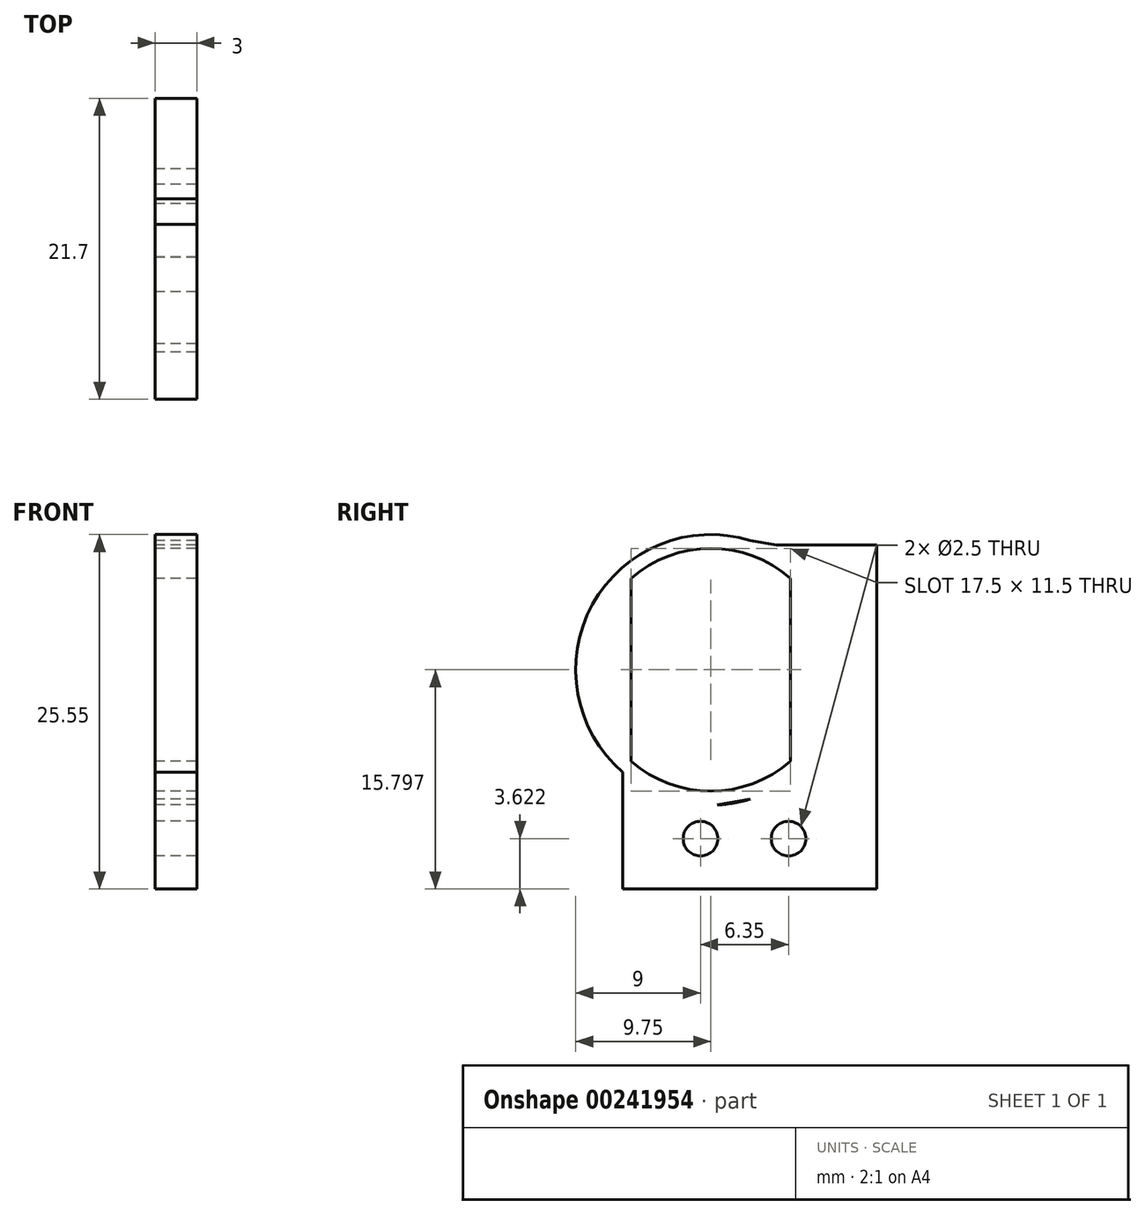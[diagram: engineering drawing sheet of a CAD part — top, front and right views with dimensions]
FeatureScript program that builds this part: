
annotation { "Feature Type Name" : "Feature", "Feature Type Description" : "" }
export const myFeature = defineFeature(function(context is Context, id is Id, definition is map)
    precondition{}
    {
        {
            var Q0;
            Q0=qCreatedBy(makeId("Right.planeOp"),FACE);
            var sketch = newSketch(context, id + "F0", { "sketchPlane" : qUnion([Q0])});
            skLineSegment(sketch, "E0", {"start": v(-11.95, -13.7) * mm, "end": v(-11.95, -5.31) * mm});
            skCircle(sketch, "E1", {"center": v(-5.6, 2.09) * mm, "radius": 9.75 * mm});
            skCircle(sketch, "E2", {"center": v(-5.6, 2.09) * mm, "radius": 8.75 * mm});
            skLineSegment(sketch, "E3", {"start": v(-5.6, 2.09) * mm, "end": v(6.35, 2.09) * mm, "construction": true});
            skLineSegment(sketch, "E4", {"start": v(-0.03, 10.09) * mm, "end": v(5.35, 10.09) * mm});
            skLineSegment(sketch, "E5", {"start": v(5.35, 10.09) * mm, "end": v(5.35, 2.09) * mm});
            skLineSegment(sketch, "E6.MirrorCS", {"start": v(5.35, -5.91) * mm, "end": v(5.35, 2.09) * mm});
            skLineSegment(sketch, "E7.MirrorCS", {"start": v(-0.03, -5.91) * mm, "end": v(5.35, -5.91) * mm});
            skLineSegment(sketch, "E8.0", {"start": v(-0.9, -6.91) * mm, "end": v(6.35, -6.91) * mm});
            skLineSegment(sketch, "E8.1", {"start": v(6.35, -6.91) * mm, "end": v(6.35, 2.09) * mm});
            skLineSegment(sketch, "E8.2", {"start": v(6.35, 11.09) * mm, "end": v(6.35, 2.09) * mm});
            skLineSegment(sketch, "E8.3", {"start": v(-0.9, 11.09) * mm, "end": v(6.35, 11.09) * mm});
            skLineSegment(sketch, "E9", {"start": v(-0.9, 11.09) * mm, "end": v(-5.13, 11.83) * mm});
            skLineSegment(sketch, "E10.MirrorCS", {"start": v(-0.9, -6.91) * mm, "end": v(-5.13, -7.65) * mm});
            skLineSegment(sketch, "E11", {"start": v(5.35, 8.12) * mm, "end": v(6.35, 8.12) * mm});
            skLineSegment(sketch, "E12.MirrorCS", {"start": v(5.35, -3.95) * mm, "end": v(6.35, -3.95) * mm});
            skLineSegment(sketch, "E13", {"start": v(-0.03, 10.09) * mm, "end": v(-2.99, 10.44) * mm});
            skLineSegment(sketch, "E14.MirrorCS", {"start": v(-0.03, -5.91) * mm, "end": v(-2.99, -6.26) * mm});
            skLineSegment(sketch, "E15", {"start": v(6.35, -6.91) * mm, "end": v(6.35, -13.7) * mm});
            skLineSegment(sketch, "E16", {"start": v(-11.95, -13.7) * mm, "end": v(6.35, -13.7) * mm});
            skCircle(sketch, "E17", {"center": v(-6.35, -10.09) * mm, "radius": 1.25 * mm});
            skCircle(sketch, "E18", {"center": v(0, -10.09) * mm, "radius": 1.25 * mm});
            skLineSegment(sketch, "E19", {"start": v(-11.35, -4.5) * mm, "end": v(-11.35, 8.68) * mm});
            skLineSegment(sketch, "E20", {"start": v(-5.6, 10.84) * mm, "end": v(-5.6, -6.66) * mm, "construction": true});
            skLineSegment(sketch, "E21.MirrorCS", {"start": v(0.15, -4.5) * mm, "end": v(0.15, 8.68) * mm});
            skSolve(sketch);
        }
        {
            var Q0;
            Q0 = qSketchRegion(id + "F0", true);
            var Q1;
            {var subQ0=sQuery(id+"F0.wireOp",EDGE,"E13");Q1=makeQuery(id+"F0.imprint","IMPRINT",FACE,{"disambiguationData":[TD([[makeQuery(id+"F0.imprint","IMPRINT",EDGE,{"derivedFrom":subQ0}),1.0]])]});}
            var Q2;
            {var subQ4=sQuery(id+"F0.wireOp",EDGE,"E4");Q2=makeQuery(id+"F0.imprint","IMPRINT",FACE,{"disambiguationData":[TD([[makeQuery(id+"F0.imprint","IMPRINT",EDGE,{"derivedFrom":subQ4}),-1.0]])]});}
            var Q3;
            {var subQ0=sQuery(id+"F0.wireOp",EDGE,"E19");Q3=makeQuery(id+"F0.imprint","IMPRINT",FACE,{"disambiguationData":[TD([[makeQuery(id+"F0.imprint","IMPRINT",EDGE,{"derivedFrom":subQ0}),1.0]])]});}
            var Q4;
            {var subQ0=sQuery(id+"F0.wireOp",EDGE,"E21.MirrorCS");Q4=makeQuery(id+"F0.imprint","IMPRINT",FACE,{"disambiguationData":[TD([[makeQuery(id+"F0.imprint","IMPRINT",EDGE,{"derivedFrom":subQ0}),-1.0]])]});}
            var Q5;
            {var subQ0=sQuery(id+"F0.wireOp",EDGE,"E10.MirrorCS");var subQ1=sQuery(id+"F0.wireOp",EDGE,"E1");var subQ2=makeQuery(id+"F0.imprint","INTERSECT",VERTEX,{"disambiguationData":[OD(0.0)],"derivedFrom":[subQ1,subQ0]});Q5=makeQuery(id+"F0.imprint","IMPRINT",FACE,{"disambiguationData":[TD([[makeQuery(id+"F0.imprint","IMPRINT",EDGE,{"disambiguationData":[TD([[subQ2,-1.0]])],"derivedFrom":subQ1}),1.0]])]});}
            extrude(context, id + "F1", {"entities" : qUnion([Q0, Q1, Q2, Q3, Q4, Q5]), "depth" : 3 * mm});
        }
    });
